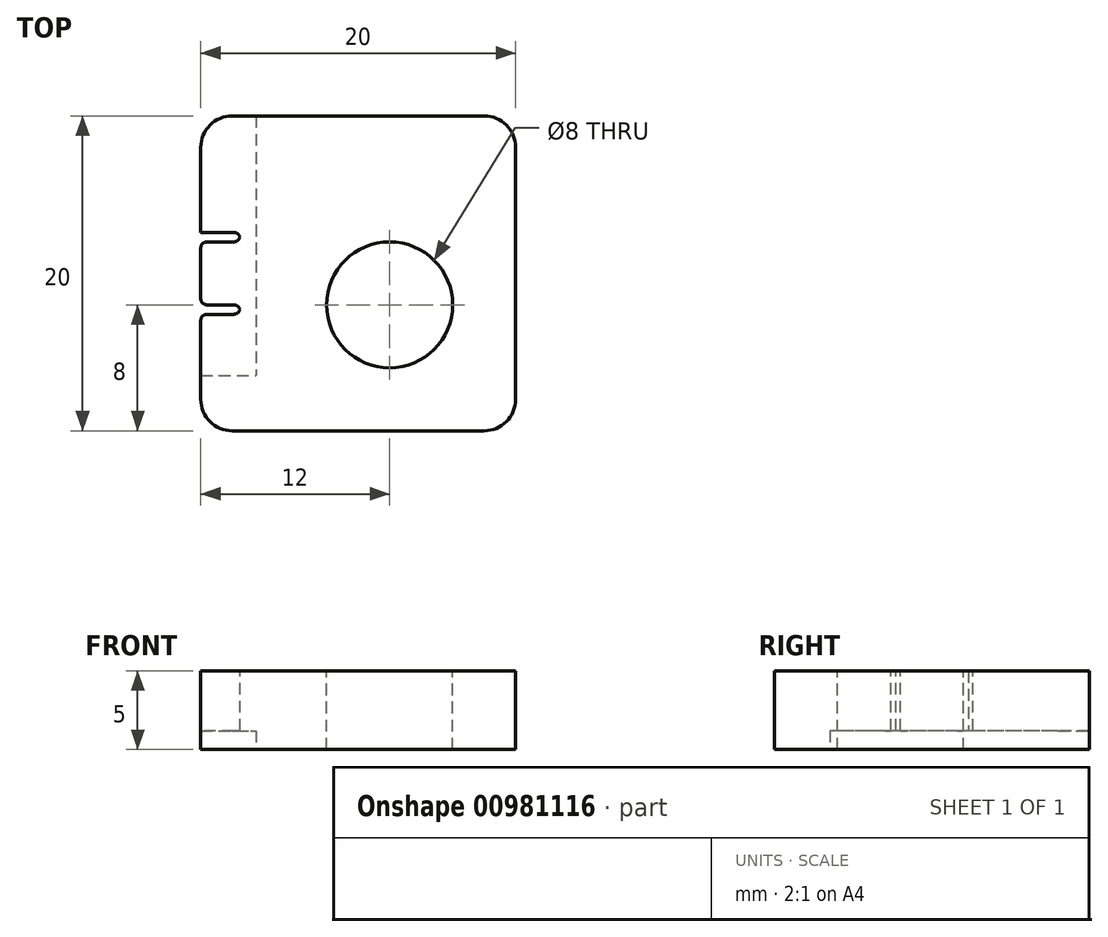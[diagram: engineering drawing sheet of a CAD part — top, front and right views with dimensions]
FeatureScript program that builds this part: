
annotation { "Feature Type Name" : "Feature", "Feature Type Description" : "" }
export const myFeature = defineFeature(function(context is Context, id is Id, definition is map)
    precondition{}
    {
        {
            var Q0;
            Q0=qCreatedBy(makeId("Top.planeOp"),FACE);
            var sketch = newSketch(context, id + "F0", { "sketchPlane" : qUnion([Q0])});
            skLineSegment(sketch, "E0.bottom", {"start": v(-10, 10) * mm, "end": v(10, 10) * mm});
            skLineSegment(sketch, "E0.top", {"start": v(-10, -10) * mm, "end": v(10, -10) * mm});
            skLineSegment(sketch, "E0.left", {"start": v(-10, 10) * mm, "end": v(-10, -10) * mm});
            skLineSegment(sketch, "E0.right", {"start": v(10, 10) * mm, "end": v(10, -10) * mm});
            skPoint(sketch, "E0.middle", {"position": v(0, 0) * mm});
            skSolve(sketch);
        }
        {
            var Q0;
            Q0=makeQuery(id+"F0.imprint","IMPRINT",FACE,{"disambiguationData":[TD([[makeQuery(id+"F0.imprint","IMPRINT",EDGE,{"derivedFrom":sQuery(id+"F0.wireOp",EDGE,"E0.bottom")}),-1.0]])]});
            extrude(context, id + "F1", {"entities" : qUnion([Q0]), "depth" : 5 * mm, "offsetDistance" : 25 * mm});
        }
        {
            var Q0;
            Q0=makeQuery(id+"F1.opExtrude","CAP_FACE",FACE,{"disambiguationData":[OSD([sQuery(id+"F0.wireOp",EDGE,"E0.bottom"),sQuery(id+"F0.wireOp",EDGE,"E0.top"),sQuery(id+"F0.wireOp",EDGE,"E0.left"),sQuery(id+"F0.wireOp",EDGE,"E0.right")])],"isStart":true});
            var sketch = newSketch(context, id + "F2", { "sketchPlane" : qUnion([Q0])});
            skLineSegment(sketch, "E1.bottom", {"start": v(-10, -10) * mm, "end": v(-6.5, -10) * mm});
            skLineSegment(sketch, "E1.top", {"start": v(-10, 6.5) * mm, "end": v(-6.5, 6.5) * mm});
            skLineSegment(sketch, "E1.left", {"start": v(-10, -10) * mm, "end": v(-10, 6.5) * mm});
            skLineSegment(sketch, "E1.right", {"start": v(-6.5, -10) * mm, "end": v(-6.5, 6.5) * mm});
            skSolve(sketch);
        }
        {
            var Q0;
            Q0=makeQuery(id+"F2.imprint","IMPRINT",FACE,{"disambiguationData":[TD([[makeQuery(id+"F2.imprint","IMPRINT",EDGE,{"derivedFrom":sQuery(id+"F2.wireOp",EDGE,"E1.bottom")}),1.0]])]});
            extrude(context, id + "F3", {"entities" : qUnion([Q0]), "operationType" : NewBodyOperationType.REMOVE, "oppositeDirection" : true, "depth" : 1.2 * mm, "offsetDistance" : 25 * mm});
        }
        {
            var Q0;
            Q0=makeQuery(id+"F1.opExtrude","CAP_FACE",FACE,{"disambiguationData":[OSD([sQuery(id+"F0.wireOp",EDGE,"E0.bottom"),sQuery(id+"F0.wireOp",EDGE,"E0.top"),sQuery(id+"F0.wireOp",EDGE,"E0.left"),sQuery(id+"F0.wireOp",EDGE,"E0.right")])],"isStart":false});
            var sketch = newSketch(context, id + "F4", { "sketchPlane" : qUnion([Q0])});
            skCircle(sketch, "E2", {"center": v(2, -2) * mm, "radius": 4 * mm});
            skSolve(sketch);
        }
        {
            var Q0;
            Q0 = qSketchRegion(id + "F4", true);
            extrude(context, id + "F5", {"entities" : qUnion([Q0]), "operationType" : NewBodyOperationType.REMOVE, "endBound" : BoundingType.THROUGH_ALL, "oppositeDirection" : true, "depth" : 25 * mm, "offsetDistance" : 25 * mm});
        }
        {
            var Q0;
            Q0=makeQuery(id+"F1.opExtrude","SWEPT_EDGE",EDGE,{"disambiguationData":[OSD([sQuery(id+"F0.wireOp",EDGE,"E0.top"),sQuery(id+"F0.wireOp",EDGE,"E0.right")])]});
            var Q1;
            Q1=makeQuery(id+"F1.opExtrude","SWEPT_EDGE",EDGE,{"disambiguationData":[OSD([sQuery(id+"F0.wireOp",EDGE,"E0.top"),sQuery(id+"F0.wireOp",EDGE,"E0.left")])]});
            var Q2;
            Q2=makeQuery(id+"F1.opExtrude","SWEPT_EDGE",EDGE,{"disambiguationData":[OSD([sQuery(id+"F0.wireOp",EDGE,"E0.bottom"),sQuery(id+"F0.wireOp",EDGE,"E0.left")])]});
            var Q3;
            Q3=makeQuery(id+"F1.opExtrude","SWEPT_EDGE",EDGE,{"disambiguationData":[OSD([sQuery(id+"F0.wireOp",EDGE,"E0.bottom"),sQuery(id+"F0.wireOp",EDGE,"E0.right")])]});
            fillet(context, id + "F6", {"entities" : qUnion([Q0, Q1, Q2, Q3]), "radius" : 2 * mm, "tangentPropagation" : true, "allowEdgeOverflow" : false});
        }
        {
            var Q0;
            Q0=makeQuery(id+"F1.opExtrude","SWEPT_FACE",FACE,{"disambiguationData":[OSD([sQuery(id+"F0.wireOp",EDGE,"E0.left")])]});
            var sketch = newSketch(context, id + "F7", { "sketchPlane" : qUnion([Q0])});
            skLineSegment(sketch, "E3", {"start": v(0, 5) * mm, "end": v(0, 0) * mm, "construction": true});
            skLineSegment(sketch, "E4.bottom", {"start": v(-2.6, 1.2) * mm, "end": v(-2, 1.2) * mm});
            skLineSegment(sketch, "E4.top", {"start": v(-2.6, 5) * mm, "end": v(-2, 5) * mm});
            skLineSegment(sketch, "E4.left", {"start": v(-2.6, 1.2) * mm, "end": v(-2.6, 5) * mm});
            skLineSegment(sketch, "E4.right", {"start": v(-2, 1.2) * mm, "end": v(-2, 5) * mm});
            skLineSegment(sketch, "E5.MirrorCS", {"start": v(2.6, 1.2) * mm, "end": v(2.6, 5) * mm});
            skLineSegment(sketch, "E6.MirrorCS", {"start": v(2, 1.2) * mm, "end": v(2, 5) * mm});
            skLineSegment(sketch, "E7.MirrorCS", {"start": v(2.6, 1.2) * mm, "end": v(2, 1.2) * mm});
            skLineSegment(sketch, "E8.MirrorCS", {"start": v(2.6, 5) * mm, "end": v(2, 5) * mm});
            skSolve(sketch);
        }
        {
            var Q0;
            Q0=makeQuery(id+"F7.imprint","IMPRINT",FACE,{"disambiguationData":[TD([[makeQuery(id+"F7.imprint","IMPRINT",EDGE,{"derivedFrom":sQuery(id+"F7.wireOp",EDGE,"E4.bottom")}),1.0]])]});
            var Q1;
            Q1=makeQuery(id+"F7.imprint","IMPRINT",FACE,{"disambiguationData":[TD([[makeQuery(id+"F7.imprint","IMPRINT",EDGE,{"derivedFrom":sQuery(id+"F7.wireOp",EDGE,"E5.MirrorCS")}),1.0]])]});
            extrude(context, id + "F8", {"entities" : qUnion([Q0, Q1]), "operationType" : NewBodyOperationType.REMOVE, "oppositeDirection" : true, "depth" : 2.5 * mm, "offsetDistance" : 25 * mm});
        }
        {
            var Q0;
            Q0=makeQuery(id+"F8.boolean.opBoolean","COPY",EDGE,{"derivedFrom":makeQuery(id+"F8.opExtrude","CAP_EDGE",EDGE,{"disambiguationData":[OSD([sQuery(id+"F7.wireOp",EDGE,"E4.right")])],"isStart":true})});
            var Q1;
            Q1=makeQuery(id+"F8.boolean.opBoolean","COPY",EDGE,{"derivedFrom":makeQuery(id+"F8.opExtrude","CAP_EDGE",EDGE,{"disambiguationData":[OSD([sQuery(id+"F7.wireOp",EDGE,"E6.MirrorCS")])],"isStart":true})});
            var Q2;
            Q2=makeQuery(id+"F8.boolean.opBoolean","COPY",EDGE,{"derivedFrom":makeQuery(id+"F8.opExtrude","CAP_EDGE",EDGE,{"disambiguationData":[OSD([sQuery(id+"F7.wireOp",EDGE,"E5.MirrorCS")])],"isStart":true})});
            var Q3;
            Q3=makeQuery(id+"F8.boolean.opBoolean","COPY",EDGE,{"derivedFrom":makeQuery(id+"F8.opExtrude","CAP_EDGE",EDGE,{"disambiguationData":[OSD([sQuery(id+"F7.wireOp",EDGE,"E4.left")])],"isStart":true})});
            var Q4;
            Q4=makeQuery(id+"F8.boolean.opBoolean","COPY",EDGE,{"derivedFrom":makeQuery(id+"F8.opExtrude","CAP_EDGE",EDGE,{"disambiguationData":[OSD([sQuery(id+"F7.wireOp",EDGE,"E4.left")])],"isStart":false})});
            var Q5;
            Q5=makeQuery(id+"F8.boolean.opBoolean","COPY",EDGE,{"derivedFrom":makeQuery(id+"F8.opExtrude","CAP_EDGE",EDGE,{"disambiguationData":[OSD([sQuery(id+"F7.wireOp",EDGE,"E4.right")])],"isStart":false})});
            var Q6;
            Q6=makeQuery(id+"F8.boolean.opBoolean","COPY",EDGE,{"derivedFrom":makeQuery(id+"F8.opExtrude","CAP_EDGE",EDGE,{"disambiguationData":[OSD([sQuery(id+"F7.wireOp",EDGE,"E5.MirrorCS")])],"isStart":false})});
            var Q7;
            Q7=makeQuery(id+"F8.boolean.opBoolean","COPY",EDGE,{"derivedFrom":makeQuery(id+"F8.opExtrude","CAP_EDGE",EDGE,{"disambiguationData":[OSD([sQuery(id+"F7.wireOp",EDGE,"E6.MirrorCS")])],"isStart":false})});
            fillet(context, id + "F9", {"entities" : qUnion([Q0, Q1, Q2, Q3, Q4, Q5, Q6, Q7]), "radius" : 0.4 * mm, "tangentPropagation" : true, "allowEdgeOverflow" : false});
        }
    });
